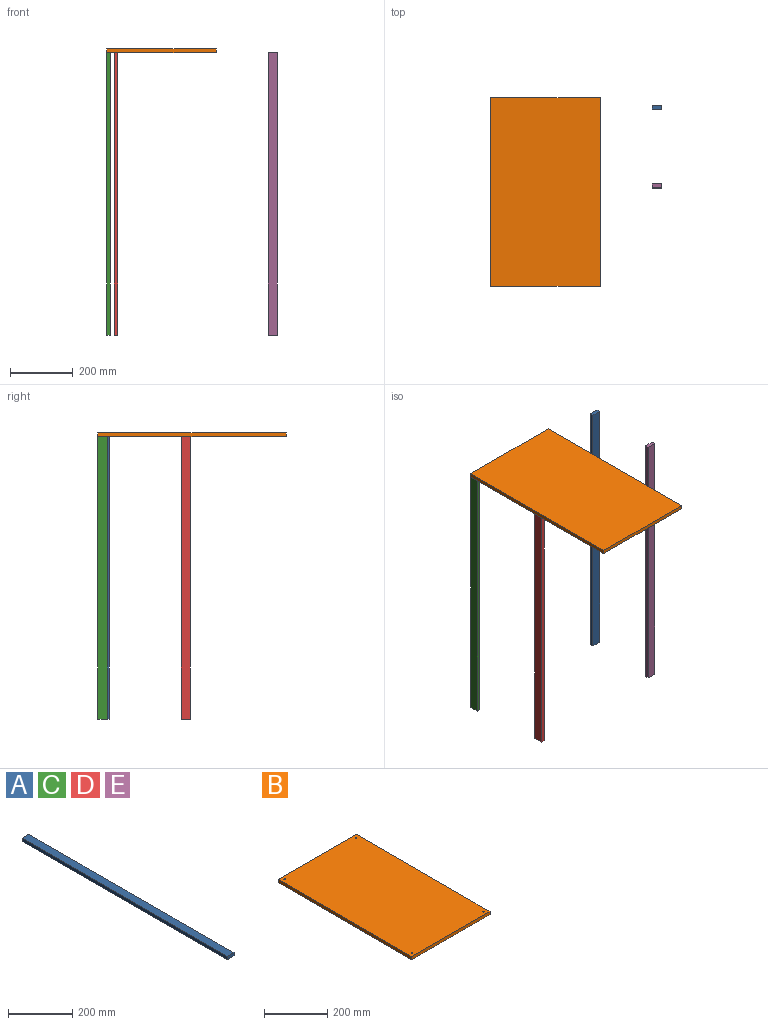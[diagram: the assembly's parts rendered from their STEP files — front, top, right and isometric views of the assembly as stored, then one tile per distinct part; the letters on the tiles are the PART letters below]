
ASSEMBLY  parts=5 mates=1
PART A: 6 faces, bbox 30x900x12 mm
  f0: plane 900x12mm, normal (-1,0,0), area 10800mm2, adj f1,f3,f4,f5
  f1: plane 30x12mm, normal (0,-1,0), area 360mm2, adj f0,f2,f4,f5
  f2: plane 900x12mm, normal (1,0,0), area 10800mm2, adj f1,f3,f4,f5
  f3: plane 30x12mm, normal (0,1,0), area 360mm2, adj f0,f2,f4,f5
  f4: plane 900x30mm, normal (0,0,1), area 27000mm2, adj f0,f1,f2,f3
  f5: plane 900x30mm, normal (0,0,-1), area 27000mm2, adj f0,f1,f2,f3
PART B: 14 faces, bbox 350x600x12 mm
  f0: plane 600x12mm, normal (-1,0,0), area 7200mm2, adj f1,f3,f4,f5
  f1: plane 350x12mm, normal (0,-1,0), area 4200mm2, adj f0,f2,f4,f5
  f2: plane 600x12mm, normal (1,0,0), area 7200mm2, adj f1,f3,f4,f5
  f3: plane 350x12mm, normal (0,1,0), area 4200mm2, adj f0,f2,f4,f5
  f4: plane 600x350mm, normal (0,0,1), area 209921.5mm2, adj f0,f1,f2,f3,f6,f8,f10,f12
  f5: plane 600x350mm, normal (0,0,-1), area 210000mm2, adj f0,f1,f2,f3
  f6: cylinder r=2.5mm len=5mm, axis (0,0,1), area 78.5mm2, adj f4,f7
  f7: plane 5x5mm, normal (0,0,1), area 19.6mm2, adj f6
  f8: cylinder r=2.5mm len=5mm, axis (0,0,1), area 78.5mm2, adj f4,f9
  f9: plane 5x5mm, normal (0,0,1), area 19.6mm2, adj f8
  f10: cylinder r=2.5mm len=5mm, axis (0,0,1), area 78.5mm2, adj f4,f11
  f11: plane 5x5mm, normal (0,0,1), area 19.6mm2, adj f10
  f12: cylinder r=2.5mm len=5mm, axis (0,0,1), area 78.5mm2, adj f4,f13
  f13: plane 5x5mm, normal (0,0,1), area 19.6mm2, adj f12
PART C: same geometry as A
PART D: same geometry as A
PART E: same geometry as A
PLACE A rot(axis=(1,0,0),90deg) t=(44.25,572.46,-624.39)mm
PLACE B rot(axis=(-1,0,0),180deg) t=(-470.75,1596.46,287.61)mm
PLACE C rot(axis=(0.58,-0.58,-0.58),120deg) t=(-458.75,596.46,-624.39)mm
PLACE D rot(axis=(0.58,-0.58,-0.58),120deg) t=(-434.75,331.46,-624.39)mm
PLACE E rot(axis=(1,0,0),90deg) t=(44.25,322.46,-624.39)mm
MATE fastened C.f3 <-> B.f4  axis (0,0,1) through (-470.75,596.46,275.61)mm
